# Revit family: QF_ELECTROLUXPROFESSIONAL_1LSNJ8_IC64821LF_G
name_source: partatom
category: Attrezzature speciali
units: mm (PartAtom-declared; Revit-internal decimal feet)

## family parameters
Basato su piano di lavoro = No
Condiviso = No
Punto di calcolo locali = No
Quota connettore circolare = Usa diametro
Sempre verticale = Sì
Taglio con vuoti quando caricato = No
Tipo di parte = Normale

## types (6) — shared parameters
Depth Actual = 1110 mm  [stored 3.64173 ft]
Gas KW = 44
Height Actual = 1270 mm  [stored 4.16667 ft]
Latent Heat Output = 0.0
Length Actual = 2775 mm  [stored 9.10433 ft]
Modello = IC64821LF
Phase = 3
Produttore = Electrolux Professional
Sensible Heat Output = 0.0
URL = www.electroluxprofessional.com
Watts = 1400 W
Weight = 810
zero-valued in all types: Prospetto di default, Steam Pounds per Hour

## per-type parameters (varying)
| type | Cycle | Descrizione | Item Number | Volts |
| 9882030160 | 50 Hz | IRONER CYLINDER IC64821LF LENGTH FOLDING 2120MM PERFORMANCE GAS CE 400/50/3 DUBIXIUM ML VAC.FEED.TABLE DIAMMS | 1L0GSR | 400 V |
| 9882030163 | 50 Hz | IRONER CYLINDER IC64821LF LENGTH FOLDING 2120MM PERFORMANCE GAS CE 400/50/3 DUBIXIUM FR VAC.FEED.TABLE DIAMMS | 1L0GSU | 400 V |
| 9882030270 | 60 Hz | IRONER CYLINDER IC64821LF LENGTH FOLDING 2120MM ACTIVE GAS CE 208-240/60/3 6MM SST CYL. EN, ES, PO FEED NOW | 1L0H4A | 240 V |
| 9882030156 | 50 Hz | IRONER CYLINDER IC64821LF LENGTH FOLDING 2120MM ACTIVE GAS CE 400/50/3 6MM SST CYL. FR FEED NOW | 1L0GSL | 400 V |
| 9882030159 | 50 Hz | IRONER CYLINDER IC64821LF LENGTH FOLDING 2120MM ACTIVE GAS CE 400/50/3 6MM SST CYL. ML FEED NOW | 1L0GSP | 400 V |
| 9882030311 | 50 Hz | IRONER CYLINDER IC64821LF LENGTH FOLDING 2120MM SUPERIOR GAS CE 400/50/3 DUBIXIUM FR FEED ALONE VAC.FEED.TABLE ANTISTATI | 1LT69Z | 400 V |

note: [stored X ft] marks values corroborated as IEEE doubles in the binary element streams (Revit-internal decimal feet)

## geometry (parser evidence)
native form markers: Sweep x9
no freeform markers — native parametric forms only
